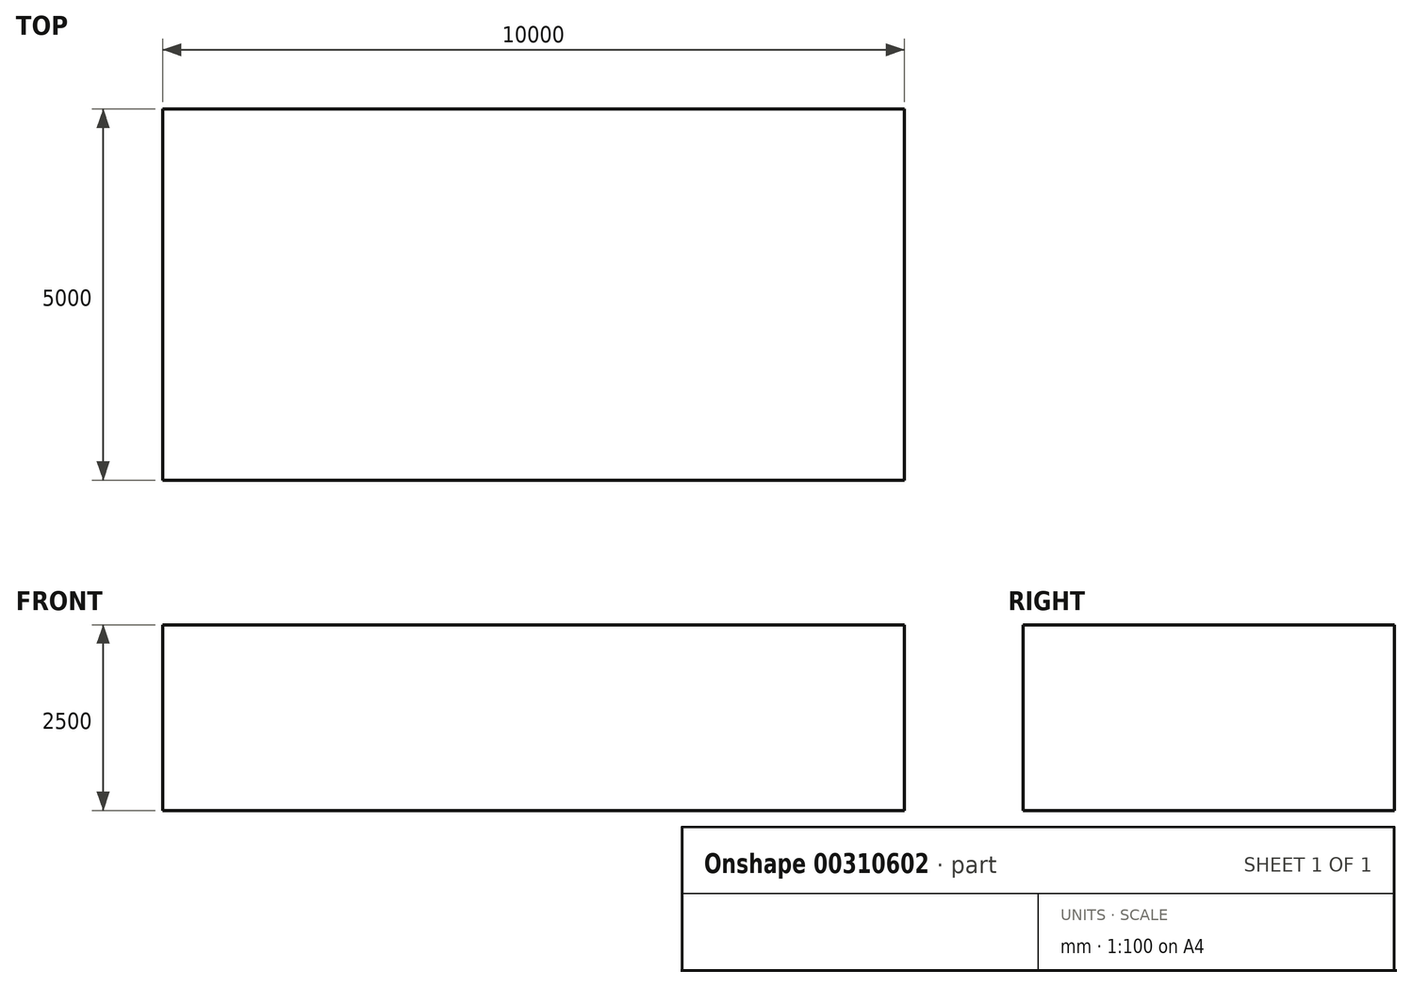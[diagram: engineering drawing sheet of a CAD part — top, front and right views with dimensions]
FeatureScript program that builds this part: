
annotation { "Feature Type Name" : "Feature", "Feature Type Description" : "" }
export const myFeature = defineFeature(function(context is Context, id is Id, definition is map)
    precondition{}
    {
        {
            var Q0;
            Q0=qCreatedBy(makeId("Top.planeOp"),FACE);
            var sketch = newSketch(context, id + "F0", { "sketchPlane" : qUnion([Q0])});
            skLineSegment(sketch, "E0.bottom", {"start": v(0, 0) * mm, "end": v(-10000, 0) * mm});
            skLineSegment(sketch, "E0.top", {"start": v(0, 5000) * mm, "end": v(-10000, 5000) * mm});
            skLineSegment(sketch, "E0.left", {"start": v(0, 0) * mm, "end": v(0, 5000) * mm});
            skLineSegment(sketch, "E0.right", {"start": v(-10000, 0) * mm, "end": v(-10000, 5000) * mm});
            skSolve(sketch);
        }
        {
            var Q0;
            Q0=makeQuery(id+"F0.imprint","IMPRINT",FACE,{"disambiguationData":[TD([[makeQuery(id+"F0.imprint","IMPRINT",EDGE,{"derivedFrom":sQuery(id+"F0.wireOp",EDGE,"E0.bottom")}),-1.0]])]});
            extrude(context, id + "F1", {"entities" : qUnion([Q0]), "depth" : 2500 * mm});
        }
    });
